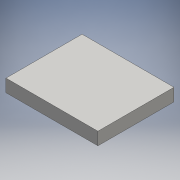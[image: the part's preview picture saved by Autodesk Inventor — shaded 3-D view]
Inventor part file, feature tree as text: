
AUTODESK INVENTOR PART (.ipt)
format: ipt  version: 2016 (Build 200138000, 138)  size: 83,968 bytes
history: native  units: mm
features: extrude x1, sketch x1
ambient origin geometry x8: Origin, YZ Plane, XZ Plane, XY Plane, X Axis, Y Axis, Z Axis, Center Point
bodies: Solid1 (feature_tree)
feature tree (2):
  extrude  "Extrusion1"  Depth=48.0mm
  sketch  "Sketch1"  dims[d0=58.0mm d1=48.0mm d2=8.0mm d3=0.0mm]
